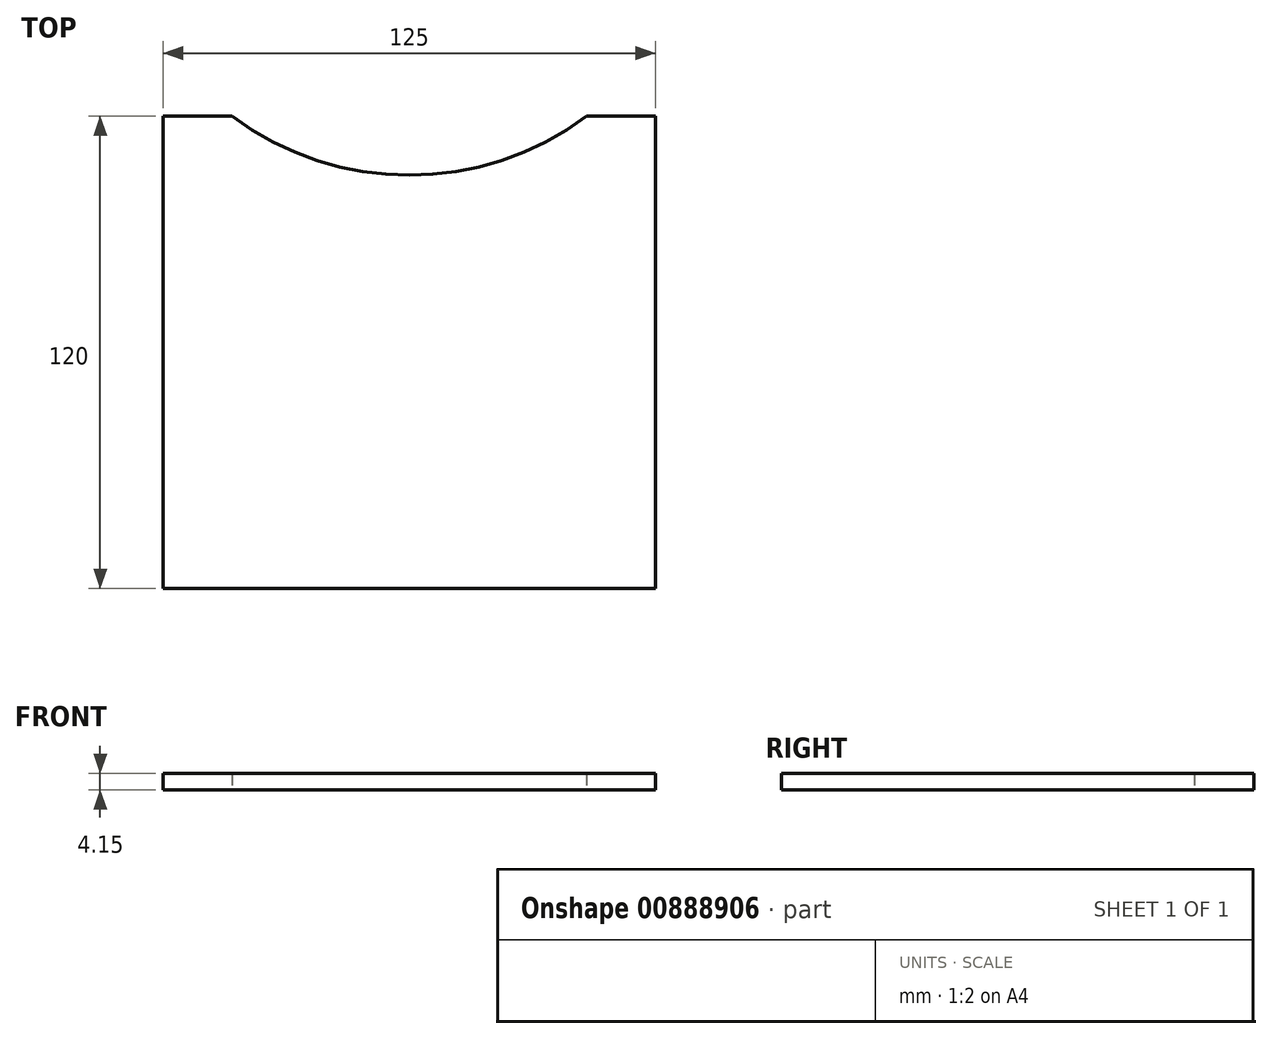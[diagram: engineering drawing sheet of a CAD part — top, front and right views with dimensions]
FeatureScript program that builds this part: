
annotation { "Feature Type Name" : "Feature", "Feature Type Description" : "" }
export const myFeature = defineFeature(function(context is Context, id is Id, definition is map)
    precondition{}
    {
        {
            var Q0;
            Q0=qCreatedBy(makeId("Top.planeOp"),FACE);
            var sketch = newSketch(context, id + "F0", { "sketchPlane" : qUnion([Q0])});
            skArc(sketch, "E0", {"start": v(-45, -60) * mm, "mid": v(0, -75) * mm, "end": v(45, -60) * mm});
            skLineSegment(sketch, "E1", {"start": v(-62.5, -60) * mm, "end": v(-45, -60) * mm});
            skLineSegment(sketch, "E2", {"start": v(-62.5, -60) * mm, "end": v(-62.5, -180) * mm});
            skLineSegment(sketch, "E3", {"start": v(-62.5, -180) * mm, "end": v(62.5, -180) * mm});
            skLineSegment(sketch, "E4", {"start": v(62.5, -180) * mm, "end": v(62.5, -60) * mm});
            skLineSegment(sketch, "E5.trimOffspring", {"start": v(45, -60) * mm, "end": v(62.5, -60) * mm});
            skSolve(sketch);
        }
        {
            var Q0;
            Q0 = qSketchRegion(id + "F0", true);
            extrude(context, id + "F1", {"entities" : qUnion([Q0]), "depth" : 4.15 * mm, "offsetDistance" : 25 * mm});
        }
    });
